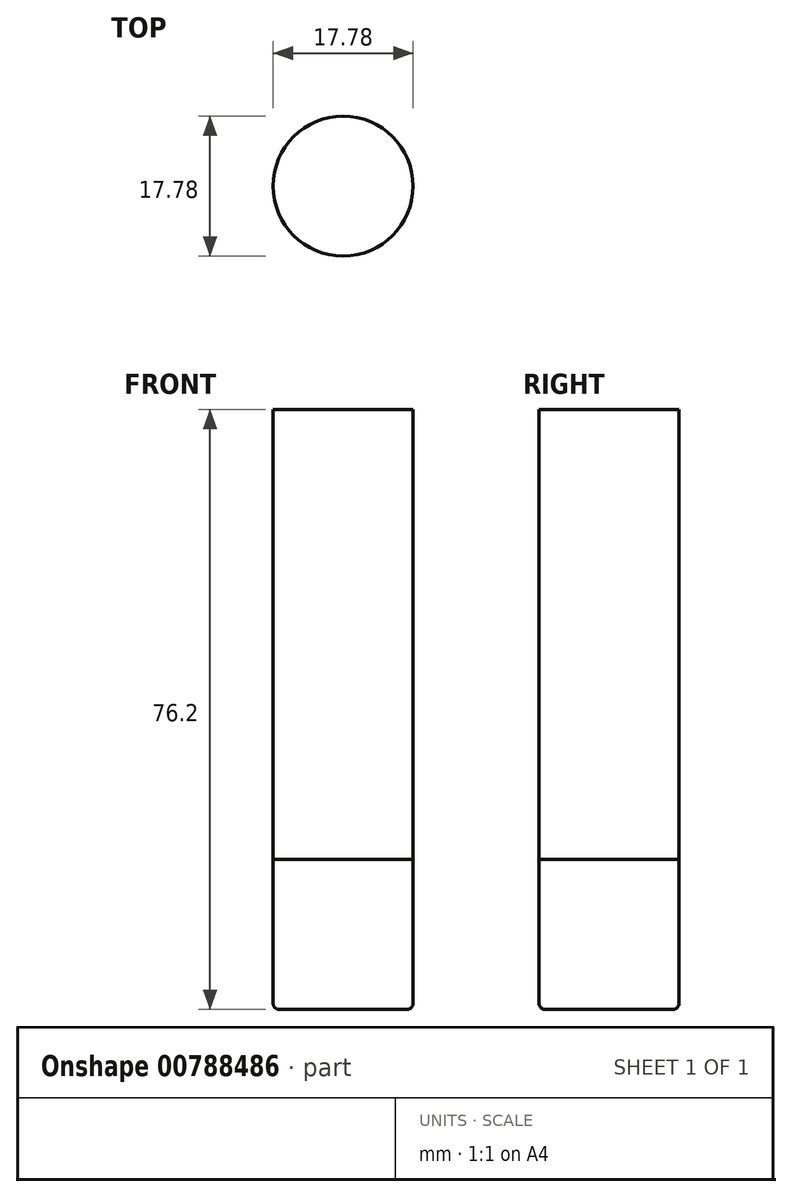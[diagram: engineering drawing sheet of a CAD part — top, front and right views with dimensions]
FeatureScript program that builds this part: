
annotation { "Feature Type Name" : "Feature", "Feature Type Description" : "" }
export const myFeature = defineFeature(function(context is Context, id is Id, definition is map)
    precondition{}
    {
        {
            var Q0;
            Q0=qCreatedBy(makeId("Front.planeOp"),FACE);
            var sketch = newSketch(context, id + "F0", { "sketchPlane" : qUnion([Q0])});
            skLineSegment(sketch, "E0", {"start": v(0, 0) * mm, "end": v(8.9, 0) * mm});
            skLineSegment(sketch, "E1", {"start": v(8.9, 0) * mm, "end": v(8.9, -75.44) * mm});
            skLineSegment(sketch, "E2", {"start": v(8.13, -76.2) * mm, "end": v(0, -76.2) * mm});
            skLineSegment(sketch, "E3", {"start": v(0, -76.2) * mm, "end": v(0, -57.15) * mm});
            skLineSegment(sketch, "E4", {"start": v(0, -57.15) * mm, "end": v(8.9, -57.15) * mm});
            skLineSegment(sketch, "E5", {"start": v(0, -57.15) * mm, "end": v(0, 0) * mm});
            skPoint(sketch, "E6.visualSharp", {"position": v(8.9, -76.2) * mm});
            skArc(sketch, "E6.filletArc", {"start": v(8.13, -76.2) * mm, "mid": v(8.67, -75.98) * mm, "end": v(8.9, -75.44) * mm});
            skSolve(sketch);
        }
        {
            var Q0;
            Q0=makeQuery(id+"F0.imprint","IMPRINT",FACE,{"disambiguationData":[TD([[makeQuery(id+"F0.imprint","IMPRINT",EDGE,{"derivedFrom":sQuery(id+"F0.wireOp",EDGE,"E2")}),-1.0]])]});
            var Q1;
            Q1=sQuery(id+"F0.wireOp",EDGE,"E3");
            revolve(context, id + "F1", {"entities" : qUnion([Q0]), "axis" : qUnion([Q1]), "revolveType" : RevolveType.FULL});
        }
        {
            var Q0;
            {var subQ0=sQuery(id+"F0.wireOp",EDGE,"E0");Q0=makeQuery(id+"F0.imprint","IMPRINT",FACE,{"disambiguationData":[TD([[makeQuery(id+"F0.imprint","IMPRINT",EDGE,{"derivedFrom":subQ0}),-1.0]])]});}
            var Q1;
            Q1=sQuery(id+"F0.wireOp",EDGE,"E5");
            revolve(context, id + "F2", {"entities" : qUnion([Q0]), "axis" : qUnion([Q1]), "revolveType" : RevolveType.FULL});
        }
    });
